# Revit family: IS_UltraFlatS_Multiproduct_BIM_IT_KV169BJ;KV169FS;KV169FR;KV169FT;KV169FV;KV169FU
name_source: partatom
category: Plumbing Fixtures
revit_build: Autodesk Revit 2015 (Build: 20140606_1530(x64)
units: mm (PartAtom-declared; Revit-internal decimal feet)

## types (6) — shared parameters
Accessori = www.idealstandard.it
AltezzaNominale = 2 mm  [stored 0.00656168 ft]
Assembly Code = C1030200
Autore = Ideal Standard Italia
Brand = Ideal Standard
Colore = Bianco
Connessione = Installazione
DescrizioneClassifcazioneUni2015 = Shower trays
Dimensione = 123 x 123 x 2 mm
Finitura = Bianco
Garanzia = Garanzia Idealstandard
IfcEsportaCome = IfcSanitaryTerminalType
InformaziniGaranzia = www.idealstandard.it/garanzia.html
InformazioniDiProdotto = www.idealstandard.it/prodotti/html
InformazioniGaranzia = www.idealstandard.it/garanzia.html
InstruzioniInstallazione = www.idealstandard.it/prodotti/html
LarghezzaNominale = 123 mm
LunghezzaNominale = 123 mm
PesoNetto = 0 Kg
PiattoDoccia = No
Produttore = www.idealstandard.it
RiferimentoClassificazioneUni2015 = Pr_40_20_06_84
Spazio = interno
Telefono = 800 652 290
TipoEspotazioneIfc = Shower trays
URL = www.idealstandard.it
UnitàDurata = anni
UnitàDurataGaranzia = anni
UnitàVolume = Litri
Versione = 1
VersioneClassificazioneUni2015 = Products v1.1
zero-valued in all types: CWFU, Cost, CostoDiSostituzione, Default Elevation, DimensioneScarico, HWFU, ProfonditàNominale, SpessoreDelMateriale, WFU

## per-type parameters (varying)
| type | Description | Material | Model | ModelloDiRiferimento | Nome | NomeOggettoBim | NumeroDiModello |
| KV169BJ - ULTRA FLAT S COPRI PILETTA ACCIAIO | Ultra Flat S Copri Piletta Acciaio | IS_RenderMaterial_Chrome - Polished | KV169BJ | Ultra Flat S Copri Piletta Acciaio | ShowerTrays_Ultraflat_KV169BJ_IdealStandard | ISI_IdealStandard_ShowerTrays_Ultraflat_KV169BJ | KV169BJ |
| KV169FT - ULTRAFLAT S GRIGLIA DI SCARICO SABBIA | Ultraflat S Griglia Di Scarico Sabbia | ISI_IdealStandard_ShowerTray_Sand_Render | KV169FT | Ultraflat S Griglia Di Scarico Sabbia | ShowerTrays_Ultraflat_KV169FT_IdealStandard | ISI_IdealStandard_ShowerTrays_Ultraflat_KV169FT | KV169FT |
| KV169FV - ULTRAFLAT S GRIGLIA DI SCARICO NERA | Ultraflat S Griglia Di Scarico Nera | ISI_IdealStandard_ShowerTray_Black_Render | KV169FV | Ultraflat S Griglia Di Scarico Nera | ShowerTrays_Ultraflat_KV169FV_IdealStandard | ISI_IdealStandard_ShowerTrays_Ultraflat_KV169FV | KV169FV |
| KV169FR - ULTRAFLAT S GRIGLIA DI SCARICO BIANCA | Ultraflat S Griglia Di Scarico Bianca | IS_RenderMaterial_VitreousChina | KV169FR | Ultraflat S Griglia Di Scarico Bianca | ShowerTrays_Ultraflat_KV169FR_IdealStandard | ISI_IdealStandard_ShowerTrays_Ultraflat_KV169FR | KV169FR |
| KV169FU - ULTRAFLAT S GRIGLIA DI SCARICO MOKA | Ultraflat S Griglia Di Scarico Moka | ISI_IdealStandard_ShowerTray_Moka_Render | KV169FU | Ultraflat S Griglia Di Scarico Moka | ShowerTrays_Ultraflat_KV169FU_IdealStandard | ISI_IdealStandard_ShowerTrays_Ultraflat_KV169FU | KV169FU |
| KV169FS - ULTRAFLAT S GRIGLIA DI GRIGIO CEMENTO | Ultraflat S Griglia Di Grigio Cemento | ISI_IdealStandard_ShowerTray_Grey_Render | KV169FS | Ultraflat S Griglia Di Grigio Cemento | ShowerTrays_Ultraflat_KV169FS_IdealStandard | ISI_IdealStandard_ShowerTrays_Ultraflat_KV169FS | KV169FS |

note: [stored X ft] marks values corroborated as IEEE doubles in the binary element streams (Revit-internal decimal feet)

## geometry (parser evidence)
native form markers: Blend x2, Sweep x1
no freeform markers — native parametric forms only
